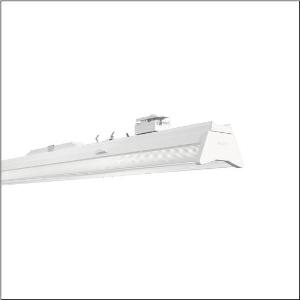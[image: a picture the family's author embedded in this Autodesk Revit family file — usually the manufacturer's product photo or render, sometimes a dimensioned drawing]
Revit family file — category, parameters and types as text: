
# Revit family: licross_21_performance_mo_52td167n46xg
name_source: partatom
category: Lighting Fixtures
units: mm (PartAtom-declared; Revit-internal decimal feet)

## family parameters
Cut with Voids When Loaded = No
Host = Face
Light Source = No
Part Type = Normal
Room Calculation Point = No
Round Connector Dimension = Use Diameter
Shared = No

## types (1)
- Licross 21 Performance MO (1 x LED, 6000 lm, 32.4 W, 4000K)
    Apparent Load = 32 VA
    CIE Flux Codes = 66 88 96 79 100
    Color Rendering = 80
    Color Temperature = 4000K
    Default Elevation = 1800 mm
    Description = Licross 21 Performance MO, luminaire insert, of sheet steel, galvanised, coil coated, white, length: 1.500mm, width: 120mm, height: 123mm, LED rated luminous flux: 6.000lm, light colour: 840, SDCM (Standard Deviation of Colour Matching)MacAdam ≤ 3 SDCM (initial), control gear: ON/OFF, with plug, 3-pole, with phase selection, mains connection: 220..240V, AC, 50/60Hz, rated input power: 32W, internal wiring halogen-free, primary light control with lens, of plastic, primary optical cover: cover, of PMMA, light emission: direct/indirect distribution, primary light characteristic: symmetric, protection rating (complete): IP54, insulation class (complete): insulation class I (protective earthing), certification: CE, ENEC, UKCA, protection symbol: D if used in an environment with non-conductive dust loads with corresponding accessories, impact resistance: IK06, permissible ambient temperature for indoor applications: -35..+50°C, corresponds to IFS (International Featured Standards) requirements for safety and quality in the food industry, reducing of maximum allowable ambient temperature of 5°C with ceiling mounting, LABS conformity tested according to VDMA 24364:2018-05, The light source and the operating device comply with the requirements of the Ecodesign Regulation (EU) 2019/2020 and are replaceable in accordance with this regulation, packaging unit: 1 piece
    Height = 114 mm
    Lamp = 1 x LED
    Lamp Light Flux = 6000 lm
    Lamp Power = 32.4 W
    Lamp count = 1
    Length = 1500 mm
    Luminous efficacy = 185 lm/W
    Manufacturer = Siteco
    ModVariant = No
    Model = 52TD167N46XG
    Mounting Place = Ceiling
    Mounting Type = Pendant
    Number of Poles = 1
    OnlyDefault = Yes
    Power Factor = 1
    Product Name = Licross 21 Performance MO
    Product group = luminaire insert | ceiling pendant
    ProductGroupID = 901
    Protection Class = Protection class I
    Protection Degree = IP 54
    RLX_Detail_Level = 1
    RLX_Emergency_Light_Flux = 0 lm
    RLX_Emergency_Type = 0
    RLX_Emergency_Type_DB = No
    RlxData = <blob elided: 30661 chars, md5=5a60d881>
    Socket = socket
    Standby Power = 0 W
    System Light Flux = 6000 lm
    System Power = 32 W
    Type Comments = Product without accessories
    Type Image = l_1256138.jpg
    URL = http://relux.com
    VarID = ---
    Voltage = 0 V
    Weight = 0.00 kg
    Width = 120 mm

## geometry (parser evidence)
native form markers: Blend x4, Sweep x11
no freeform markers — native parametric forms only
